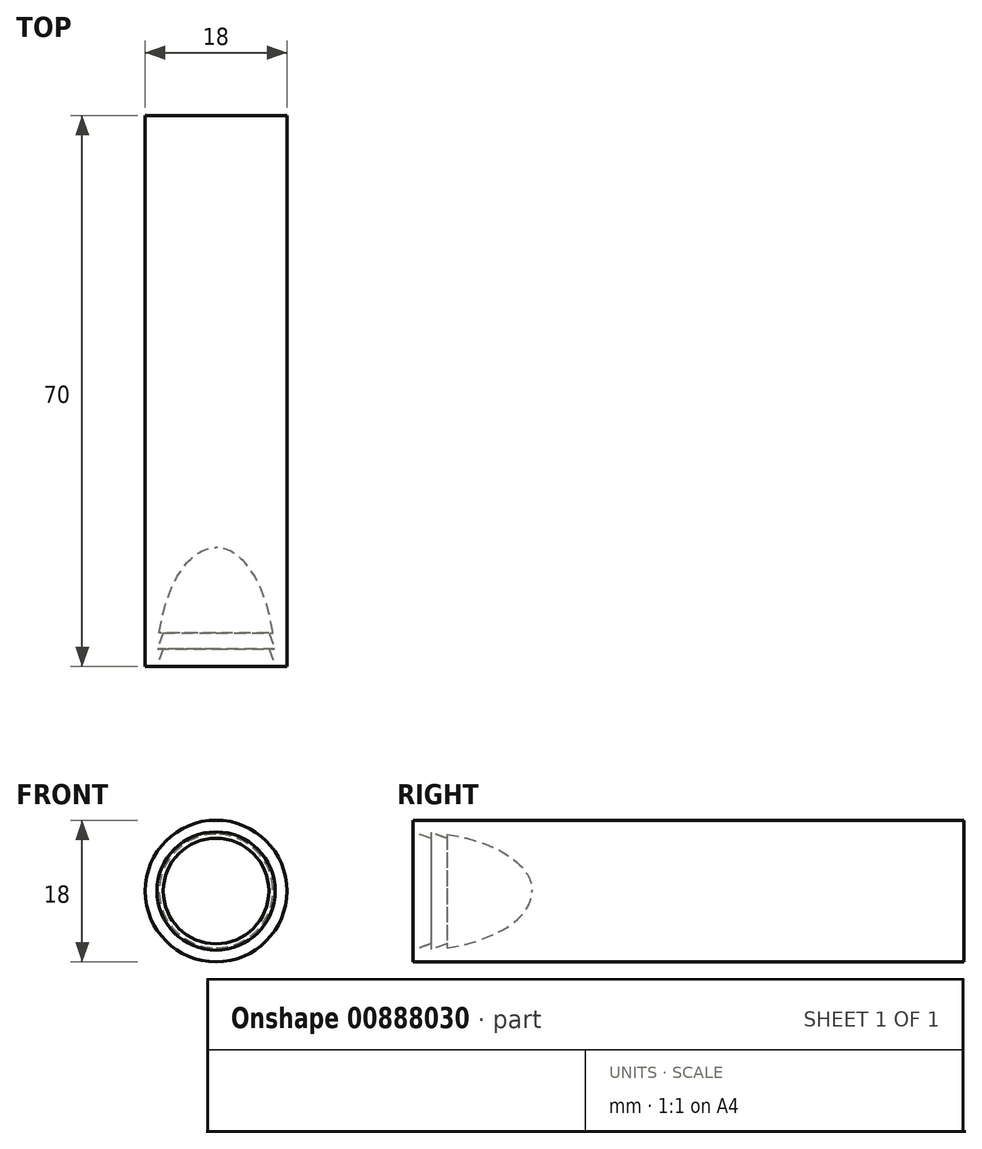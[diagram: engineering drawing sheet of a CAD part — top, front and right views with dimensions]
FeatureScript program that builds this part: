
annotation { "Feature Type Name" : "Feature", "Feature Type Description" : "" }
export const myFeature = defineFeature(function(context is Context, id is Id, definition is map)
    precondition{}
    {
        {
            var Q0;
            Q0=qCreatedBy(makeId("Front.planeOp"),FACE);
            var sketch = newSketch(context, id + "F0", { "sketchPlane" : qUnion([Q0])});
            skCircle(sketch, "E0", {"center": v(0, 0) * mm, "radius": 9 * mm});
            skSolve(sketch);
        }
        {
            var Q0;
            Q0=qSketchRegion(id+"F0",true);
            extrude(context, id + "F1", {"entities" : qUnion([Q0]), "depth" : 70 * mm, "offsetDistance" : 25 * mm});
        }
        {
            var Q0;
            Q0=qCreatedBy(makeId("Right.planeOp"),FACE);
            var sketch = newSketch(context, id + "F2", { "sketchPlane" : qUnion([Q0])});
            skEllipticalArc(sketch, "E1", {});
            skLineSegment(sketch, "E2.bottom", {"start": v(-70.05, 0) * mm, "end": v(-67.73, 0) * mm});
            skLineSegment(sketch, "E2.left", {"start": v(-70.05, 0) * mm, "end": v(-70.05, -7.53) * mm});
            skLineSegment(sketch, "E2.right", {"start": v(-67.73, -6.7) * mm, "end": v(-67.73, -7.44) * mm});
            skLineSegment(sketch, "E3.bottom", {"start": v(-67.73, 0) * mm, "end": v(-65.7, 0) * mm});
            skLineSegment(sketch, "E3.right", {"start": v(-65.7, -6.7) * mm, "end": v(-65.7, -7.22) * mm});
            skLineSegment(sketch, "E4", {"start": v(-70.05, -7.53) * mm, "end": v(-67.73, -6.7) * mm});
            skLineSegment(sketch, "E5", {"start": v(-67.73, -7.44) * mm, "end": v(-65.7, -6.7) * mm});
            skLineSegment(sketch, "E6", {"start": v(-65.7, 0) * mm, "end": v(-54.87, 0) * mm});
            skPoint(sketch, "E7.orphan", {"position": v(-65.7, -9.1) * mm});
            skPoint(sketch, "E8.orphan", {"position": v(-67.73, -9.1) * mm});
            const initialGuessF2  = {"E1": [-0.0700518861413002, 0, 1, 0, 0.01518334448337555, 0.007532604251627598, 5.003567198051183, 0]};
            skSetInitialGuess(sketch, initialGuessF2);
            skSolve(sketch);
        }
        {
            var Q0;
            Q0 = qSketchRegion(id + "F2", true);
            var Q1;
            Q1=sQuery(id+"F2.wireOp",EDGE,"E6");
            revolve(context, id + "F3", {"operationType" : NewBodyOperationType.REMOVE, "surfaceOperationType" : NewSurfaceOperationType.NEW, "entities" : qUnion([Q0]), "axis" : qUnion([Q1]), "revolveType" : RevolveType.FULL, "oppositeDirection" : true});
        }
    });
